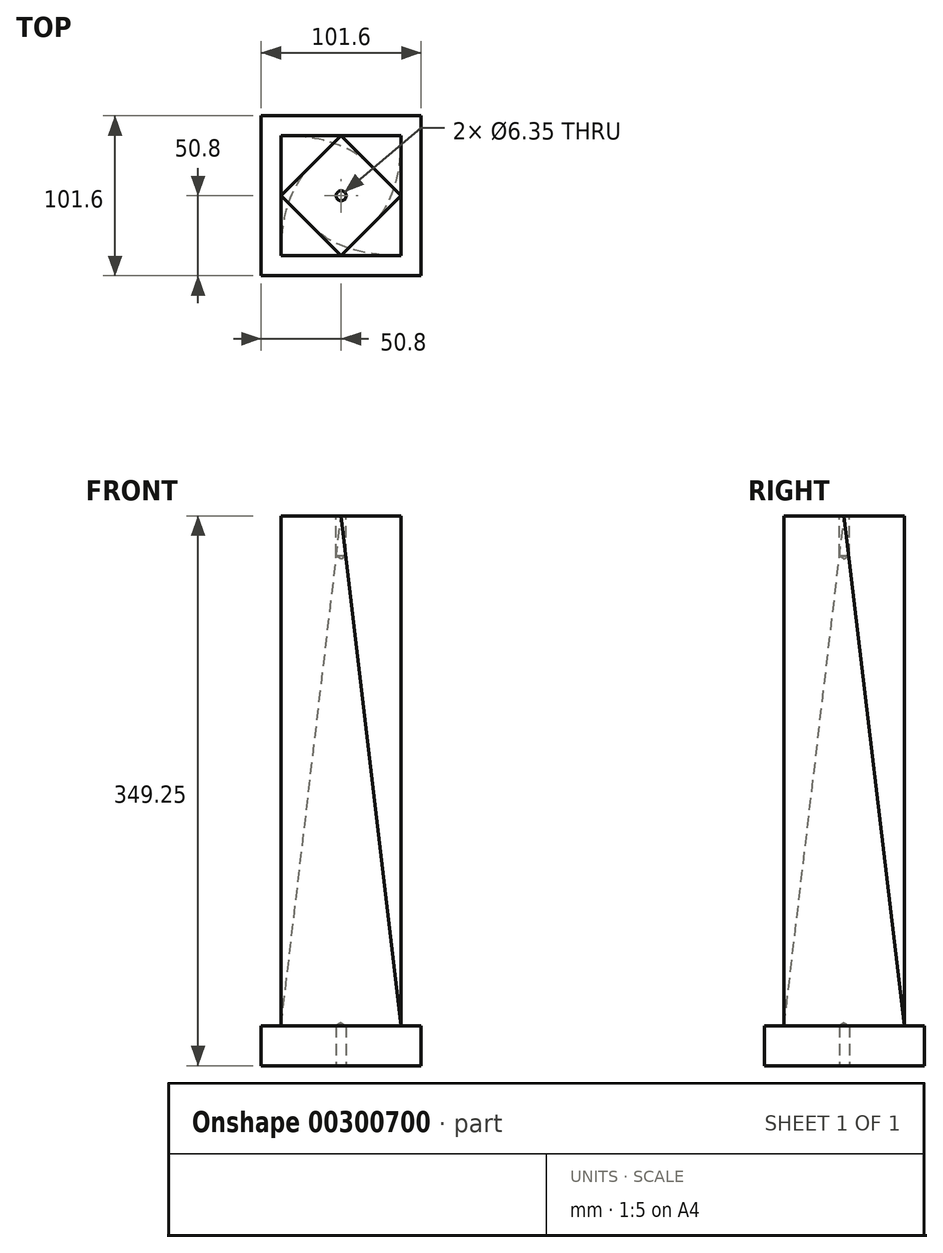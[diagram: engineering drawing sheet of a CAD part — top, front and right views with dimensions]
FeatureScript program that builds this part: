
annotation { "Feature Type Name" : "Feature", "Feature Type Description" : "" }
export const myFeature = defineFeature(function(context is Context, id is Id, definition is map)
    precondition{}
    {
        {
            var Q0;
            Q0=qCreatedBy(makeId("Top.planeOp"),FACE);
            var sketch = newSketch(context, id + "F0", { "sketchPlane" : qUnion([Q0])});
            skLineSegment(sketch, "E0", {"start": v(0, 0) * mm, "end": v(101.6, 0) * mm});
            skLineSegment(sketch, "E1", {"start": v(101.6, 0) * mm, "end": v(101.6, -101.6) * mm});
            skLineSegment(sketch, "E2", {"start": v(101.6, -101.6) * mm, "end": v(0, -101.6) * mm});
            skLineSegment(sketch, "E3", {"start": v(0, -101.6) * mm, "end": v(0, 0) * mm});
            skPoint(sketch, "E4", {"position": v(50.8, -50.8) * mm});
            skPoint(sketch, "E4.positionSnap0", {"position": v(0, -50.8) * mm});
            skPoint(sketch, "E4.positionSnap1", {"position": v(50.8, 0) * mm});
            skSolve(sketch);
        }
        {
            var Q0;
            Q0 = qSketchRegion(id + "F0", true);
            extrude(context, id + "F1", {"entities" : qUnion([Q0]), "depth" : 25.4 * mm});
        }
        {
            var Q0;
            Q0=makeQuery(id+"F1.opExtrude","CAP_FACE",FACE,{"disambiguationData":[OSD([sQuery(id+"F0.wireOp",EDGE,"E0"),sQuery(id+"F0.wireOp",EDGE,"E1"),sQuery(id+"F0.wireOp",EDGE,"E2"),sQuery(id+"F0.wireOp",EDGE,"E3"),sQuery(id+"F0.wireOp",EDGE,"UEuqQQuo-Hkgc-hHoz-7Im5-4zg91TPoVtWk"),sQuery(id+"F0.wireOp",EDGE,"oUBJdOqv-h60D-aRWc-B2CP-wXNexcqYv7ms"),sQuery(id+"F0.wireOp",EDGE,"XaE4gdaR-w1WS-HY8Y-b6qO-hQf7LSbeCRj1"),sQuery(id+"F0.wireOp",EDGE,"wNpe2BvY-wa0S-eaSe-UWrr-Ks6aLOfGlq8B")])],"isStart":false});
            var sketch = newSketch(context, id + "F2", { "sketchPlane" : qUnion([Q0])});
            skLineSegment(sketch, "E5", {"start": v(12.7, -12.7) * mm, "end": v(88.9, -12.7) * mm});
            skLineSegment(sketch, "E6", {"start": v(88.9, -12.7) * mm, "end": v(88.9, -88.9) * mm});
            skLineSegment(sketch, "E7", {"start": v(88.9, -88.9) * mm, "end": v(12.7, -88.9) * mm});
            skLineSegment(sketch, "E8", {"start": v(12.7, -88.9) * mm, "end": v(12.7, -12.7) * mm});
            skSolve(sketch);
        }
        {
            var Q0;
            Q0=qCreatedBy(makeId("Top.planeOp"),FACE);
            cPlane(context, id + "F3", {"entities" : qUnion([Q0]), "cplaneType" : CPlaneType.OFFSET, "offset" : 349.25 * mm, "width" : 152.4 * mm, "height" : 152.4 * mm});
        }
        {
            var Q0;
            Q0=qCreatedBy(id+"F3.planeOp",FACE);
            var sketch = newSketch(context, id + "F4", { "sketchPlane" : qUnion([Q0])});
            skLineSegment(sketch, "E9", {"start": v(12.7, -50.8) * mm, "end": v(50.8, -12.7) * mm});
            skLineSegment(sketch, "E10", {"start": v(50.8, -12.7) * mm, "end": v(88.9, -50.8) * mm});
            skLineSegment(sketch, "E11", {"start": v(88.9, -50.8) * mm, "end": v(50.8, -88.9) * mm});
            skLineSegment(sketch, "E12", {"start": v(50.8, -88.9) * mm, "end": v(12.7, -50.8) * mm});
            skPoint(sketch, "E13.orphan", {"position": v(88.9, -88.9) * mm});
            skPoint(sketch, "E14.orphan", {"position": v(88.9, -12.7) * mm});
            skPoint(sketch, "E15.orphan", {"position": v(12.7, -12.7) * mm});
            skPoint(sketch, "E16.start.orphan", {"position": v(12.7, -88.9) * mm});
            skPoint(sketch, "E17", {"position": v(50.8, -50.8) * mm});
            skSolve(sketch);
        }
        {
            var Q1;
            Q1=makeQuery(id+"F2.imprint","IMPRINT",FACE,{"disambiguationData":[TD([[makeQuery(id+"F2.imprint","IMPRINT",EDGE,{"derivedFrom":sQuery(id+"F2.wireOp",EDGE,"E5")}),-1.0]])]});
            var Q2;
            Q2=makeQuery(id+"F4.imprint","IMPRINT",FACE,{"disambiguationData":[TD([[makeQuery(id+"F4.imprint","IMPRINT",EDGE,{"derivedFrom":sQuery(id+"F4.wireOp",EDGE,"E9")}),-1.0]])]});
            loft(context, id + "F5", {"operationType" : NewBodyOperationType.ADD, "sheetProfilesArray" : [{ "sheetProfileEntities" : qUnion([Q1]) }, { "sheetProfileEntities" : qUnion([Q2]) }]});
        }
        {
            var Q0;
            Q0=sQuery(id+"F0.wireOp",VERTEX,"E4");
            var Q1;
            Q1=sQuery(id+"F4.wireOp",VERTEX,"E17");
            var Q2;
            Q2=makeQuery(id+"F1.opExtrude","SWEPT_BODY",BODY,{"disambiguationData":[OSD([sQuery(id+"F0.wireOp",EDGE,"E0"),sQuery(id+"F0.wireOp",EDGE,"E1"),sQuery(id+"F0.wireOp",EDGE,"E2"),sQuery(id+"F0.wireOp",EDGE,"E3")])]});
            hole(context, id + "F6", {"style" : HoleStyle.SIMPLE, "endStyle" : HoleEndStyle.BLIND, "oppositeDirection" : true, "holeDiameter" : 6.35 * mm, "holeDepth" : 25.4 * mm, "tappedDepth" : 12.7 * mm, "tapClearance" : 3, "locations" : qUnion([Q0, Q1]), "scope" : qUnion([Q2])});
        }
        {
            var Q0;
            Q0=sQuery(id+"F4.wireOp",VERTEX,"E17");
            var Q1;
            Q1=makeQuery(id+"F1.opExtrude","SWEPT_BODY",BODY,{"disambiguationData":[OSD([sQuery(id+"F0.wireOp",EDGE,"E0"),sQuery(id+"F0.wireOp",EDGE,"E1"),sQuery(id+"F0.wireOp",EDGE,"E2"),sQuery(id+"F0.wireOp",EDGE,"E3")])]});
            hole(context, id + "F7", {"style" : HoleStyle.SIMPLE, "endStyle" : HoleEndStyle.BLIND, "holeDiameter" : 6.35 * mm, "holeDepth" : 25.4 * mm, "tappedDepth" : 12.7 * mm, "tapClearance" : 3, "locations" : qUnion([Q0]), "scope" : qUnion([Q1])});
        }
    });
